# Revit family: Flachverbinder 35-4 L-Form
name_source: partatom
category: HLS-Bauteile
revit_build: Autodesk Revit 2017 (Build: 20190507_1515(x64)
units: mm (PartAtom-declared; Revit-internal decimal feet)

## family parameters
Arbeitsebenenbasiert = Ja
Beim Laden mit Abzugskörper schneiden = Nein
Bemaßung runder Anschluss = Durchmesser verwenden
Gemeinsam genutzt = Ja
Immer vertikal = Nein
Raumberechnungspunkt = Nein
Teiletyp = Normal

## types (1)
- Flachverbinder 35-4 L-Form
    Artikelnummer = 0814430
    B = 35 mm
    EAN = 4250928419989
    Fabrikat = MEFA
    Firma = MEFA Befestigungs- und Montagesysteme GmbH
    Gewicht = 0.14 kg
    Gewicht pro Bauteil = 0.14 kg
    Kurztext1 = Flachverbinder L-Form
    Kurztext2 = für C-Profil 35, Stex 35 Lochung 10.5 mm
    L = 83 mm
    L1 = 80 mm
    Lochdurchmesser = 10.5 mm
    Länge Schenkel 1 = 0 mm  [stored 0 ft]
    Länge Schenkel 2 = 0 mm  [stored 0 ft]
    Material = Stahl
    Materialname = S235
    Mengeneinheit = St
    Oberflaeche = galvanisch verzinkt
    Profil = C-Profil
    Profiltyp = 35, Stex 35
    Sicherheitsfaktor = 0
    Stärke Material = 0 mm  [stored 0 ft]
    Vorgabe-Ansicht = 1219 mm
    max. Rohraußendurchmesser = 0 mm  [stored 0 ft]
    max. zul. Last Fx = 0.00 kN
    max. zul. Last Fz = 0.00 kN
    min. Rohraußendurchmesser = 0 mm  [stored 0 ft]
    vpe = 25 St

note: [stored X ft] marks values corroborated as IEEE doubles in the binary element streams (Revit-internal decimal feet)
